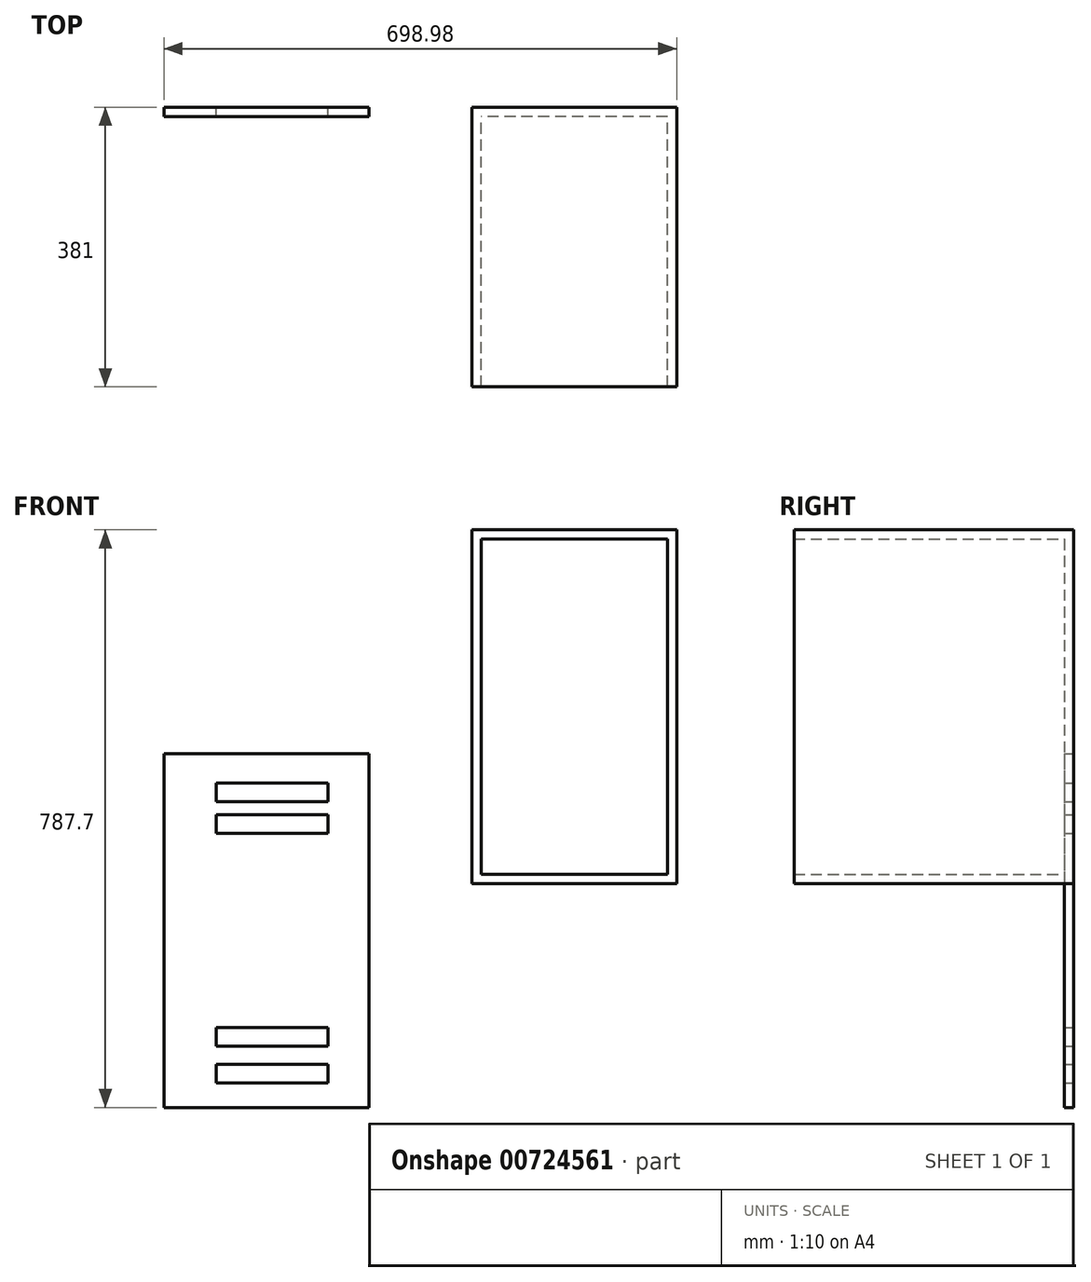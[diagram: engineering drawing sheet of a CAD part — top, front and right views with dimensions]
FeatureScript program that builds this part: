
annotation { "Feature Type Name" : "Feature", "Feature Type Description" : "" }
export const myFeature = defineFeature(function(context is Context, id is Id, definition is map)
    precondition{}
    {
        {
            var Q0;
            Q0=qCreatedBy(makeId("Front.planeOp"),FACE);
            var sketch = newSketch(context, id + "F0", { "sketchPlane" : qUnion([Q0])});
            skLineSegment(sketch, "E0.bottom", {"start": v(294.21, 454.96) * mm, "end": v(14.81, 454.96) * mm});
            skLineSegment(sketch, "E0.top", {"start": v(294.21, -27.64) * mm, "end": v(14.81, -27.64) * mm});
            skLineSegment(sketch, "E0.left", {"start": v(294.21, 454.96) * mm, "end": v(294.21, -27.64) * mm});
            skLineSegment(sketch, "E0.right", {"start": v(14.81, 454.96) * mm, "end": v(14.81, -27.64) * mm});
            skLineSegment(sketch, "E1.bottom", {"start": v(-363.23, 498.02) * mm, "end": v(-83.83, 498.02) * mm});
            skLineSegment(sketch, "E1.top", {"start": v(-363.23, 15.42) * mm, "end": v(-83.83, 15.42) * mm});
            skLineSegment(sketch, "E1.left", {"start": v(-363.23, 498.02) * mm, "end": v(-363.23, 15.42) * mm});
            skLineSegment(sketch, "E1.right", {"start": v(-83.83, 498.02) * mm, "end": v(-83.83, 15.42) * mm});
            skSolve(sketch);
        }
        {
            var Q0;
            Q0=makeQuery(id+"F0.imprint","IMPRINT",FACE,{"disambiguationData":[TD([[makeQuery(id+"F0.imprint","IMPRINT",EDGE,{"derivedFrom":sQuery(id+"F0.wireOp",EDGE,"E0.bottom")}),1.0]])]});
            extrude(context, id + "F1", {"entities" : qUnion([Q0]), "depth" : 381 * mm, "offsetDistance" : 25.4 * mm});
        }
        {
            var Q0;
            Q0=qCreatedBy(makeId("Front.planeOp"),FACE);
            var sketch = newSketch(context, id + "F2", { "sketchPlane" : qUnion([Q0])});
            skLineSegment(sketch, "E2.bottom", {"start": v(-404.77, 149.86) * mm, "end": v(-125.37, 149.86) * mm});
            skLineSegment(sketch, "E2.top", {"start": v(-404.77, -332.74) * mm, "end": v(-125.37, -332.74) * mm});
            skLineSegment(sketch, "E2.left", {"start": v(-404.77, 149.86) * mm, "end": v(-404.77, -332.74) * mm});
            skLineSegment(sketch, "E2.right", {"start": v(-125.37, 149.86) * mm, "end": v(-125.37, -332.74) * mm});
            skLineSegment(sketch, "E3.bottom", {"start": v(-333.52, 109.33) * mm, "end": v(-181.12, 109.33) * mm});
            skLineSegment(sketch, "E3.top", {"start": v(-333.52, 83.93) * mm, "end": v(-181.12, 83.93) * mm});
            skLineSegment(sketch, "E3.left", {"start": v(-333.52, 109.33) * mm, "end": v(-333.52, 83.93) * mm});
            skLineSegment(sketch, "E3.right", {"start": v(-181.12, 109.33) * mm, "end": v(-181.12, 83.93) * mm});
            skLineSegment(sketch, "E4.bottom", {"start": v(-333.52, 66.25) * mm, "end": v(-181.12, 66.25) * mm});
            skLineSegment(sketch, "E4.top", {"start": v(-333.52, 40.85) * mm, "end": v(-181.12, 40.85) * mm});
            skLineSegment(sketch, "E4.left", {"start": v(-333.52, 66.25) * mm, "end": v(-333.52, 40.85) * mm});
            skLineSegment(sketch, "E4.right", {"start": v(-181.12, 66.25) * mm, "end": v(-181.12, 40.85) * mm});
            skLineSegment(sketch, "E5.bottom", {"start": v(-333.52, -223.46) * mm, "end": v(-181.12, -223.46) * mm});
            skLineSegment(sketch, "E5.top", {"start": v(-333.52, -248.86) * mm, "end": v(-181.12, -248.86) * mm});
            skLineSegment(sketch, "E5.left", {"start": v(-333.52, -223.46) * mm, "end": v(-333.52, -248.86) * mm});
            skLineSegment(sketch, "E5.right", {"start": v(-181.12, -223.46) * mm, "end": v(-181.12, -248.86) * mm});
            skLineSegment(sketch, "E6.bottom", {"start": v(-333.52, -273.68) * mm, "end": v(-181.12, -273.68) * mm});
            skLineSegment(sketch, "E6.top", {"start": v(-333.52, -299.08) * mm, "end": v(-181.12, -299.08) * mm});
            skLineSegment(sketch, "E6.left", {"start": v(-333.52, -273.68) * mm, "end": v(-333.52, -299.08) * mm});
            skLineSegment(sketch, "E6.right", {"start": v(-181.12, -273.68) * mm, "end": v(-181.12, -299.08) * mm});
            skSolve(sketch);
        }
        {
            var Q0;
            Q0=makeQuery(id+"F2.imprint","IMPRINT",FACE,{"disambiguationData":[TD([[makeQuery(id+"F2.imprint","IMPRINT",EDGE,{"derivedFrom":sQuery(id+"F2.wireOp",EDGE,"E2.bottom")}),-1.0]])]});
            extrude(context, id + "F3", {"entities" : qUnion([Q0]), "depth" : 12.7 * mm, "offsetDistance" : 25.4 * mm});
        }
        {
            var Q0;
            Q0=makeQuery(id+"F1.opExtrude","CAP_FACE",FACE,{"disambiguationData":[OSD([sQuery(id+"F0.wireOp",EDGE,"E0.bottom"),sQuery(id+"F0.wireOp",EDGE,"E0.top"),sQuery(id+"F0.wireOp",EDGE,"E0.left"),sQuery(id+"F0.wireOp",EDGE,"E0.right")])],"isStart":false});
            shell(context, id + "F4", {"entities" : qUnion([Q0]), "thickness" : 12.7 * mm});
        }
    });
